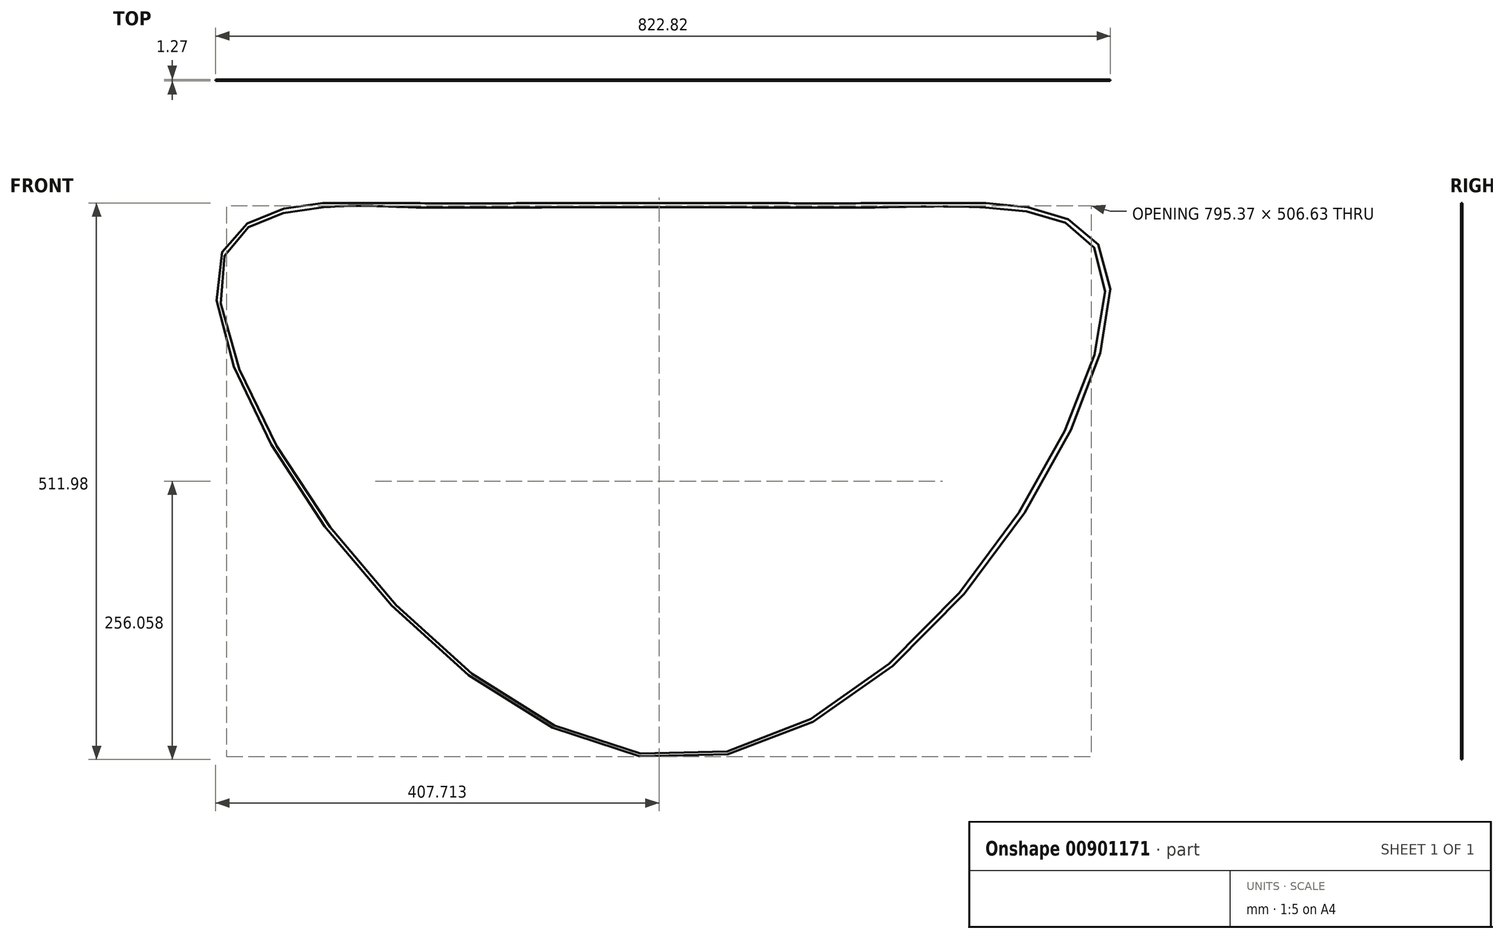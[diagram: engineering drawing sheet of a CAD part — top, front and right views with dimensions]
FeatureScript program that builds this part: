
annotation { "Feature Type Name" : "Feature", "Feature Type Description" : "" }
export const myFeature = defineFeature(function(context is Context, id is Id, definition is map)
    precondition{}
    {
        {
            var Q0;
            Q0=qCreatedBy(makeId("Front.planeOp"),FACE);
            var sketch = newSketch(context, id + "F0", { "sketchPlane" : qUnion([Q0])});
            skLineSegment(sketch, "E0", {"start": v(-304.33, 0) * mm, "end": v(305.67, 0) * mm});
            skFitSpline(sketch, "E1", {"points": [v(-304.33, 0) * mm, v(-402, -63.81) * mm, v(27.12, -511.94) * mm, v(418.6, -62.83) * mm, v(305.67, 0) * mm, v(203.78, 0) * mm, v(90.87, 0) * mm, v(-102.75, 0) * mm, v(-218.8, 0) * mm, v(-304.33, 0) * mm]});
            skLineSegment(sketch, "E2", {"start": v(305.3, -4.03) * mm, "end": v(-305.7, -4.03) * mm});
            skFitSpline(sketch, "E3", {"points": [v(305.3, -4.03) * mm, v(413.78, -63.51) * mm, v(27.09, -509.26) * mm, v(-398.58, -64.93) * mm, v(-305.7, -4.03) * mm, v(-218.33, -4.03) * mm, v(-102.83, -4.03) * mm, v(90.75, -4.03) * mm, v(203.72, -4.03) * mm, v(305.3, -4.03) * mm]});
            skSolve(sketch);
        }
        {
            var Q0;
            {var subQ7=sQuery(id+"F0.wireOp",EDGE,"E1");var subQ8=sQuery(id+"F0.wireOp",EDGE,"E0");var subQ13=makeQuery(id+"F0.imprint","INTERSECT",VERTEX,{"disambiguationData":[OD(0.0)],"derivedFrom":[subQ8,subQ7]});Q0=makeQuery(id+"F0.imprint","IMPRINT",FACE,{"disambiguationData":[TD([[makeQuery(id+"F0.imprint","IMPRINT",EDGE,{"disambiguationData":[TD([[subQ13,-1.0]])],"derivedFrom":subQ8}),-1.0]])]});}
            extrude(context, id + "F1", {"entities" : qUnion([Q0]), "depth" : 1.27 * mm, "offsetDistance" : 25.4 * mm});
        }
    });
